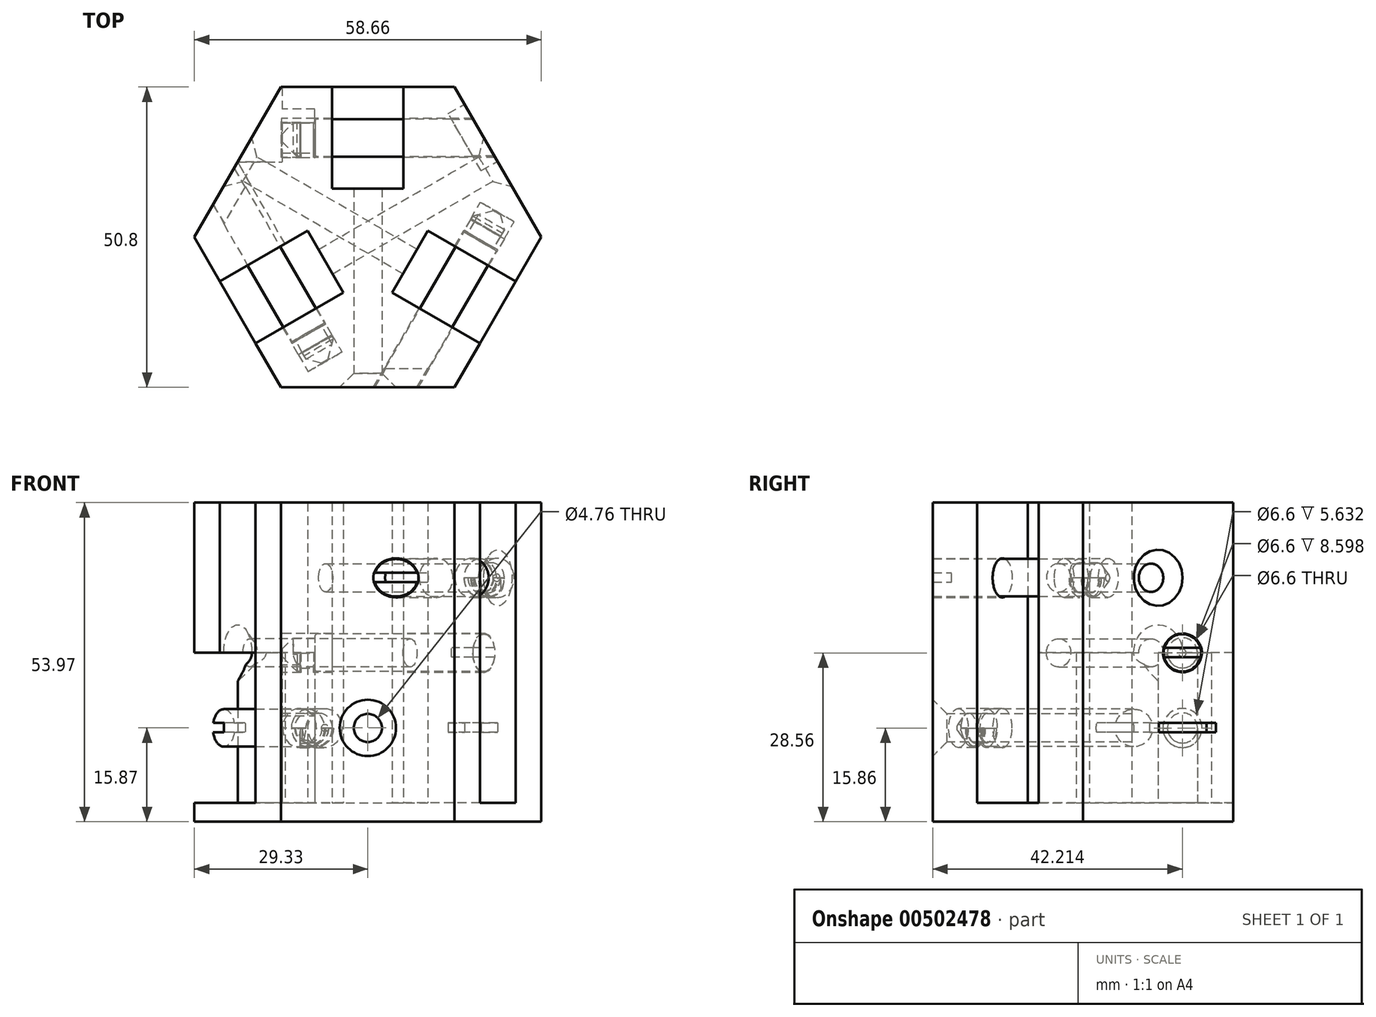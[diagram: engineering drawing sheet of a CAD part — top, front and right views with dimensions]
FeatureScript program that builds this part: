
annotation { "Feature Type Name" : "Feature", "Feature Type Description" : "" }
export const myFeature = defineFeature(function(context is Context, id is Id, definition is map)
    precondition{}
    {
        {
            var Q0;
            Q0=qCreatedBy(makeId("Top.planeOp"),FACE);
            var sketch = newSketch(context, id + "F0", { "sketchPlane" : qUnion([Q0])});
            skCircle(sketch, "E0.cCircle", {"center": v(0, 0) * mm, "radius": 25.4 * mm, "construction": true});
            skLineSegment(sketch, "E0.0", {"start": v(-14.66, 25.4) * mm, "end": v(14.66, 25.4) * mm});
            skLineSegment(sketch, "E0.1", {"start": v(14.66, 25.4) * mm, "end": v(29.33, 0) * mm});
            skLineSegment(sketch, "E0.2", {"start": v(29.33, 0) * mm, "end": v(14.66, -25.4) * mm});
            skLineSegment(sketch, "E0.3", {"start": v(14.66, -25.4) * mm, "end": v(-14.66, -25.4) * mm});
            skLineSegment(sketch, "E0.4", {"start": v(-14.66, -25.4) * mm, "end": v(-29.33, 0) * mm});
            skLineSegment(sketch, "E0.5", {"start": v(-29.33, 0) * mm, "end": v(-14.66, 25.4) * mm});
            skPoint(sketch, "E0.0.midPoint", {"position": v(0, 25.4) * mm});
            skLineSegment(sketch, "E1.0", {"start": v(0, -25.4) * mm, "end": v(-22, 12.7) * mm});
            skLineSegment(sketch, "E1.1", {"start": v(-22, 12.7) * mm, "end": v(22, 12.7) * mm});
            skLineSegment(sketch, "E1.2", {"start": v(22, 12.7) * mm, "end": v(0, -25.4) * mm});
            skLineSegment(sketch, "E2", {"start": v(0, 0) * mm, "end": v(11, -6.35) * mm, "construction": true});
            skLineSegment(sketch, "E3", {"start": v(0, 0) * mm, "end": v(0, 12.7) * mm, "construction": true});
            skLineSegment(sketch, "E4", {"start": v(0, 0) * mm, "end": v(-11, -6.35) * mm, "construction": true});
            skLineSegment(sketch, "E5", {"start": v(-25.01, -7.48) * mm, "end": v(-6.03, 3.48) * mm});
            skLineSegment(sketch, "E6", {"start": v(25.01, -7.48) * mm, "end": v(6.03, 3.48) * mm});
            skLineSegment(sketch, "E7", {"start": v(18.98, -17.92) * mm, "end": v(0, -6.97) * mm});
            skLineSegment(sketch, "E8", {"start": v(0, -6.97) * mm, "end": v(-18.98, -17.92) * mm});
            skLineSegment(sketch, "E9", {"start": v(-6.03, 3.48) * mm, "end": v(-6.03, 25.4) * mm});
            skLineSegment(sketch, "E10", {"start": v(6.03, 3.48) * mm, "end": v(6.03, 25.4) * mm});
            skCircle(sketch, "E11.cCircle", {"center": v(0, 0) * mm, "radius": 6.97 * mm, "construction": true});
            skLineSegment(sketch, "E11.0", {"start": v(0, -6.97) * mm, "end": v(-6.03, 3.48) * mm});
            skLineSegment(sketch, "E11.1", {"start": v(-6.03, 3.48) * mm, "end": v(6.03, 3.48) * mm});
            skLineSegment(sketch, "E11.2", {"start": v(6.03, 3.48) * mm, "end": v(0, -6.97) * mm});
            skLineSegment(sketch, "E12", {"start": v(-10.16, 1.1) * mm, "end": v(-4.12, -9.35) * mm});
            skLineSegment(sketch, "E13", {"start": v(4.12, -9.35) * mm, "end": v(10.16, 1.1) * mm});
            skLineSegment(sketch, "E14", {"start": v(-6.03, 8.25) * mm, "end": v(6.03, 8.25) * mm});
            skSolve(sketch);
        }
        {
            var Q0;
            {var subQ0=sQuery(id+"F0.wireOp",EDGE,"E9");var subQ1=sQuery(id+"F0.wireOp",EDGE,"E0.0");var subQ2=makeQuery(id+"F0.imprint","INTERSECT",VERTEX,{"derivedFrom":[subQ1,subQ0]});Q0=makeQuery(id+"F0.imprint","IMPRINT",FACE,{"disambiguationData":[TD([[makeQuery(id+"F0.imprint","IMPRINT",EDGE,{"disambiguationData":[TD([[subQ2,-1.0]])],"derivedFrom":subQ1}),-1.0]])]});}
            var Q1;
            {var subQ5=sQuery(id+"F0.wireOp",EDGE,"E11.1");Q1=makeQuery(id+"F0.imprint","IMPRINT",FACE,{"disambiguationData":[TD([[makeQuery(id+"F0.imprint","IMPRINT",EDGE,{"derivedFrom":subQ5}),1.0]])]});}
            var Q2;
            {var subQ0=sQuery(id+"F0.wireOp",EDGE,"E0.1");var subQ1=sQuery(id+"F0.wireOp",EDGE,"E0.0");var subQ2=makeQuery(id+"F0.imprint","INTERSECT",VERTEX,{"derivedFrom":[subQ1,subQ0]});Q2=makeQuery(id+"F0.imprint","IMPRINT",FACE,{"disambiguationData":[TD([[makeQuery(id+"F0.imprint","IMPRINT",EDGE,{"disambiguationData":[TD([[subQ2,1.0]])],"derivedFrom":subQ1}),-1.0]])]});}
            var Q3;
            {var subQ1=sQuery(id+"F0.wireOp",EDGE,"E1.1");var subQ3=sQuery(id+"F0.wireOp",EDGE,"E10");var subQ4=makeQuery(id+"F0.imprint","INTERSECT",VERTEX,{"derivedFrom":[subQ1,subQ3]});Q3=makeQuery(id+"F0.imprint","IMPRINT",FACE,{"disambiguationData":[TD([[makeQuery(id+"F0.imprint","IMPRINT",EDGE,{"disambiguationData":[TD([[subQ4,-1.0]])],"derivedFrom":subQ1}),-1.0]])]});}
            var Q4;
            {var subQ0=sQuery(id+"F0.wireOp",EDGE,"E0.2");var subQ1=sQuery(id+"F0.wireOp",EDGE,"E0.1");var subQ2=makeQuery(id+"F0.imprint","INTERSECT",VERTEX,{"derivedFrom":[subQ1,subQ0]});Q4=makeQuery(id+"F0.imprint","IMPRINT",FACE,{"disambiguationData":[TD([[makeQuery(id+"F0.imprint","IMPRINT",EDGE,{"disambiguationData":[TD([[subQ2,-1.0]])],"derivedFrom":subQ0}),-1.0]])]});}
            var Q5;
            {var subQ0=sQuery(id+"F0.wireOp",EDGE,"E6");var subQ1=sQuery(id+"F0.wireOp",EDGE,"E0.2");var subQ2=makeQuery(id+"F0.imprint","INTERSECT",VERTEX,{"derivedFrom":[subQ1,subQ0]});Q5=makeQuery(id+"F0.imprint","IMPRINT",FACE,{"disambiguationData":[TD([[makeQuery(id+"F0.imprint","IMPRINT",EDGE,{"disambiguationData":[TD([[subQ2,-1.0]])],"derivedFrom":subQ1}),-1.0]])]});}
            var Q6;
            {var subQ1=sQuery(id+"F0.wireOp",EDGE,"E1.0");var subQ3=sQuery(id+"F0.wireOp",EDGE,"E8");var subQ4=makeQuery(id+"F0.imprint","INTERSECT",VERTEX,{"derivedFrom":[subQ1,subQ3]});Q6=makeQuery(id+"F0.imprint","IMPRINT",FACE,{"disambiguationData":[TD([[makeQuery(id+"F0.imprint","IMPRINT",EDGE,{"disambiguationData":[TD([[subQ4,1.0]])],"derivedFrom":subQ1}),-1.0]])]});}
            var Q7;
            {var subQ0=sQuery(id+"F0.wireOp",EDGE,"E5");var subQ1=sQuery(id+"F0.wireOp",EDGE,"E0.4");var subQ2=makeQuery(id+"F0.imprint","INTERSECT",VERTEX,{"derivedFrom":[subQ1,subQ0]});Q7=makeQuery(id+"F0.imprint","IMPRINT",FACE,{"disambiguationData":[TD([[makeQuery(id+"F0.imprint","IMPRINT",EDGE,{"disambiguationData":[TD([[subQ2,1.0]])],"derivedFrom":subQ1}),-1.0]])]});}
            var Q8;
            {var subQ0=sQuery(id+"F0.wireOp",EDGE,"E0.5");var subQ1=sQuery(id+"F0.wireOp",EDGE,"E0.4");var subQ2=makeQuery(id+"F0.imprint","INTERSECT",VERTEX,{"derivedFrom":[subQ1,subQ0]});Q8=makeQuery(id+"F0.imprint","IMPRINT",FACE,{"disambiguationData":[TD([[makeQuery(id+"F0.imprint","IMPRINT",EDGE,{"disambiguationData":[TD([[subQ2,1.0]])],"derivedFrom":subQ1}),-1.0]])]});}
            var Q9;
            {var subQ0=sQuery(id+"F0.wireOp",EDGE,"E0.5");var subQ1=sQuery(id+"F0.wireOp",EDGE,"E0.0");var subQ2=makeQuery(id+"F0.imprint","INTERSECT",VERTEX,{"derivedFrom":[subQ1,subQ0]});Q9=makeQuery(id+"F0.imprint","IMPRINT",FACE,{"disambiguationData":[TD([[makeQuery(id+"F0.imprint","IMPRINT",EDGE,{"disambiguationData":[TD([[subQ2,-1.0]])],"derivedFrom":subQ1}),-1.0]])]});}
            var Q10;
            {var subQ0=sQuery(id+"F0.wireOp",EDGE,"E0.4");var subQ1=sQuery(id+"F0.wireOp",EDGE,"E0.3");var subQ2=makeQuery(id+"F0.imprint","INTERSECT",VERTEX,{"derivedFrom":[subQ1,subQ0]});Q10=makeQuery(id+"F0.imprint","IMPRINT",FACE,{"disambiguationData":[TD([[makeQuery(id+"F0.imprint","IMPRINT",EDGE,{"disambiguationData":[TD([[subQ2,-1.0]])],"derivedFrom":subQ0}),-1.0]])]});}
            var Q11;
            {var subQ0=sQuery(id+"F0.wireOp",EDGE,"E0.3");var subQ1=sQuery(id+"F0.wireOp",EDGE,"E0.2");var subQ2=makeQuery(id+"F0.imprint","INTERSECT",VERTEX,{"derivedFrom":[subQ1,subQ0]});Q11=makeQuery(id+"F0.imprint","IMPRINT",FACE,{"disambiguationData":[TD([[makeQuery(id+"F0.imprint","IMPRINT",EDGE,{"disambiguationData":[TD([[subQ2,1.0]])],"derivedFrom":subQ1}),-1.0]])]});}
            var Q12;
            {var subQ1=sQuery(id+"F0.wireOp",EDGE,"E1.0");var subQ3=sQuery(id+"F0.wireOp",EDGE,"E5");var subQ4=makeQuery(id+"F0.imprint","INTERSECT",VERTEX,{"derivedFrom":[subQ1,subQ3]});Q12=makeQuery(id+"F0.imprint","IMPRINT",FACE,{"disambiguationData":[TD([[makeQuery(id+"F0.imprint","IMPRINT",EDGE,{"disambiguationData":[TD([[subQ4,-1.0]])],"derivedFrom":subQ1}),-1.0]])]});}
            var Q13;
            {var subQ5=sQuery(id+"F0.wireOp",EDGE,"E11.0");Q13=makeQuery(id+"F0.imprint","IMPRINT",FACE,{"disambiguationData":[TD([[makeQuery(id+"F0.imprint","IMPRINT",EDGE,{"derivedFrom":subQ5}),1.0]])]});}
            var Q14;
            {var subQ5=sQuery(id+"F0.wireOp",EDGE,"E11.2");Q14=makeQuery(id+"F0.imprint","IMPRINT",FACE,{"disambiguationData":[TD([[makeQuery(id+"F0.imprint","IMPRINT",EDGE,{"derivedFrom":subQ5}),1.0]])]});}
            var Q15;
            Q15=makeQuery(id+"F0.imprint","IMPRINT",FACE,{"disambiguationData":[TD([[makeQuery(id+"F0.imprint","IMPRINT",EDGE,{"derivedFrom":sQuery(id+"F0.wireOp",EDGE,"E11.0")}),-1.0]])]});
            var Q16;
            Q16=makeQuery(id+"F2.opExtrude","SWEPT_FACE",FACE,{"disambiguationData":[OSD([sQuery(id+"F0.wireOp",EDGE,"E6")])]});
            var Q17;
            {var subQ5=sQuery(id+"F0.wireOp",EDGE,"E14");Q17=makeQuery(id+"F0.imprint","IMPRINT",FACE,{"disambiguationData":[TD([[makeQuery(id+"F0.imprint","IMPRINT",EDGE,{"derivedFrom":subQ5}),1.0]])]});}
            var Q18;
            {var subQ5=sQuery(id+"F0.wireOp",EDGE,"E13");Q18=makeQuery(id+"F0.imprint","IMPRINT",FACE,{"disambiguationData":[TD([[makeQuery(id+"F0.imprint","IMPRINT",EDGE,{"derivedFrom":subQ5}),-1.0]])]});}
            var Q19;
            {var subQ5=sQuery(id+"F0.wireOp",EDGE,"E12");Q19=makeQuery(id+"F0.imprint","IMPRINT",FACE,{"disambiguationData":[TD([[makeQuery(id+"F0.imprint","IMPRINT",EDGE,{"derivedFrom":subQ5}),-1.0]])]});}
            extrude(context, id + "F1", {"entities" : qUnion([Q0, Q1, Q2, Q3, Q4, Q5, Q6, Q7, Q8, Q9, Q10, Q11, Q12, Q13, Q14, Q15, Q16, Q17, Q18, Q19]), "oppositeDirection" : true, "depth" : 3.17 * mm});
        }
        {
            var Q0;
            {var subQ0=sQuery(id+"F0.wireOp",EDGE,"E0.5");var subQ1=sQuery(id+"F0.wireOp",EDGE,"E0.0");var subQ2=makeQuery(id+"F0.imprint","INTERSECT",VERTEX,{"derivedFrom":[subQ1,subQ0]});Q0=makeQuery(id+"F0.imprint","IMPRINT",FACE,{"disambiguationData":[TD([[makeQuery(id+"F0.imprint","IMPRINT",EDGE,{"disambiguationData":[TD([[subQ2,-1.0]])],"derivedFrom":subQ1}),-1.0]])]});}
            var Q1;
            {var subQ0=sQuery(id+"F0.wireOp",EDGE,"E0.1");var subQ1=sQuery(id+"F0.wireOp",EDGE,"E0.0");var subQ2=makeQuery(id+"F0.imprint","INTERSECT",VERTEX,{"derivedFrom":[subQ1,subQ0]});Q1=makeQuery(id+"F0.imprint","IMPRINT",FACE,{"disambiguationData":[TD([[makeQuery(id+"F0.imprint","IMPRINT",EDGE,{"disambiguationData":[TD([[subQ2,1.0]])],"derivedFrom":subQ1}),-1.0]])]});}
            var Q2;
            {var subQ0=sQuery(id+"F0.wireOp",EDGE,"E0.2");var subQ1=sQuery(id+"F0.wireOp",EDGE,"E0.1");var subQ2=makeQuery(id+"F0.imprint","INTERSECT",VERTEX,{"derivedFrom":[subQ1,subQ0]});Q2=makeQuery(id+"F0.imprint","IMPRINT",FACE,{"disambiguationData":[TD([[makeQuery(id+"F0.imprint","IMPRINT",EDGE,{"disambiguationData":[TD([[subQ2,-1.0]])],"derivedFrom":subQ0}),-1.0]])]});}
            var Q3;
            {var subQ0=sQuery(id+"F0.wireOp",EDGE,"E0.5");var subQ1=sQuery(id+"F0.wireOp",EDGE,"E0.4");var subQ2=makeQuery(id+"F0.imprint","INTERSECT",VERTEX,{"derivedFrom":[subQ1,subQ0]});Q3=makeQuery(id+"F0.imprint","IMPRINT",FACE,{"disambiguationData":[TD([[makeQuery(id+"F0.imprint","IMPRINT",EDGE,{"disambiguationData":[TD([[subQ2,1.0]])],"derivedFrom":subQ1}),-1.0]])]});}
            var Q4;
            {var subQ1=sQuery(id+"F0.wireOp",EDGE,"E1.1");var subQ3=sQuery(id+"F0.wireOp",EDGE,"E10");var subQ4=makeQuery(id+"F0.imprint","INTERSECT",VERTEX,{"derivedFrom":[subQ1,subQ3]});Q4=makeQuery(id+"F0.imprint","IMPRINT",FACE,{"disambiguationData":[TD([[makeQuery(id+"F0.imprint","IMPRINT",EDGE,{"disambiguationData":[TD([[subQ4,-1.0]])],"derivedFrom":subQ1}),-1.0]])]});}
            var Q5;
            {var subQ1=sQuery(id+"F0.wireOp",EDGE,"E1.0");var subQ3=sQuery(id+"F0.wireOp",EDGE,"E5");var subQ4=makeQuery(id+"F0.imprint","INTERSECT",VERTEX,{"derivedFrom":[subQ1,subQ3]});Q5=makeQuery(id+"F0.imprint","IMPRINT",FACE,{"disambiguationData":[TD([[makeQuery(id+"F0.imprint","IMPRINT",EDGE,{"disambiguationData":[TD([[subQ4,-1.0]])],"derivedFrom":subQ1}),-1.0]])]});}
            var Q6;
            {var subQ1=sQuery(id+"F0.wireOp",EDGE,"E1.0");var subQ3=sQuery(id+"F0.wireOp",EDGE,"E8");var subQ4=makeQuery(id+"F0.imprint","INTERSECT",VERTEX,{"derivedFrom":[subQ1,subQ3]});Q6=makeQuery(id+"F0.imprint","IMPRINT",FACE,{"disambiguationData":[TD([[makeQuery(id+"F0.imprint","IMPRINT",EDGE,{"disambiguationData":[TD([[subQ4,1.0]])],"derivedFrom":subQ1}),-1.0]])]});}
            var Q7;
            {var subQ0=sQuery(id+"F0.wireOp",EDGE,"E0.3");var subQ1=sQuery(id+"F0.wireOp",EDGE,"E0.2");var subQ2=makeQuery(id+"F0.imprint","INTERSECT",VERTEX,{"derivedFrom":[subQ1,subQ0]});Q7=makeQuery(id+"F0.imprint","IMPRINT",FACE,{"disambiguationData":[TD([[makeQuery(id+"F0.imprint","IMPRINT",EDGE,{"disambiguationData":[TD([[subQ2,1.0]])],"derivedFrom":subQ1}),-1.0]])]});}
            var Q8;
            {var subQ0=sQuery(id+"F0.wireOp",EDGE,"E0.4");var subQ1=sQuery(id+"F0.wireOp",EDGE,"E0.3");var subQ2=makeQuery(id+"F0.imprint","INTERSECT",VERTEX,{"derivedFrom":[subQ1,subQ0]});Q8=makeQuery(id+"F0.imprint","IMPRINT",FACE,{"disambiguationData":[TD([[makeQuery(id+"F0.imprint","IMPRINT",EDGE,{"disambiguationData":[TD([[subQ2,-1.0]])],"derivedFrom":subQ0}),-1.0]])]});}
            var Q9;
            {var subQ0=sQuery(id+"F0.wireOp",EDGE,"E11.0");Q9=makeQuery(id+"F0.imprint","IMPRINT",FACE,{"disambiguationData":[TD([[makeQuery(id+"F0.imprint","IMPRINT",EDGE,{"derivedFrom":subQ0}),1.0]])]});}
            var Q10;
            {var subQ0=sQuery(id+"F0.wireOp",EDGE,"E11.2");Q10=makeQuery(id+"F0.imprint","IMPRINT",FACE,{"disambiguationData":[TD([[makeQuery(id+"F0.imprint","IMPRINT",EDGE,{"derivedFrom":subQ0}),1.0]])]});}
            var Q11;
            {var subQ0=sQuery(id+"F0.wireOp",EDGE,"E11.1");Q11=makeQuery(id+"F0.imprint","IMPRINT",FACE,{"disambiguationData":[TD([[makeQuery(id+"F0.imprint","IMPRINT",EDGE,{"derivedFrom":subQ0}),1.0]])]});}
            var Q12;
            Q12=makeQuery(id+"F0.imprint","IMPRINT",FACE,{"disambiguationData":[TD([[makeQuery(id+"F0.imprint","IMPRINT",EDGE,{"derivedFrom":sQuery(id+"F0.wireOp",EDGE,"E11.0")}),-1.0]])]});
            extrude(context, id + "F2", {"entities" : qUnion([Q0, Q1, Q2, Q3, Q4, Q5, Q6, Q7, Q8, Q9, Q10, Q11, Q12]), "operationType" : NewBodyOperationType.ADD, "depth" : 50.8 * mm});
        }
        {
            var Q0;
            {var subQ0=sQuery(id+"F0.wireOp",EDGE,"E0.3");Q0=makeQuery(id+"F2.boolean.opBoolean","MERGE",FACE,{"derivedFrom":[makeQuery(id+"F1.opExtrude","SWEPT_FACE",FACE,{"disambiguationData":[OSD([subQ0])]}),makeQuery(id+"F2.opExtrude","SWEPT_FACE",FACE,{"disambiguationData":[OSD([subQ0])]})]});}
            var sketch = newSketch(context, id + "F3", { "sketchPlane" : qUnion([Q0])});
            skPoint(sketch, "E15", {"position": v(0, 12.7) * mm});
            skSolve(sketch);
        }
        {
            var Q0;
            {var subQ0=sQuery(id+"F0.wireOp",EDGE,"E0.1");Q0=makeQuery(id+"F2.boolean.opBoolean","MERGE",FACE,{"derivedFrom":[makeQuery(id+"F1.opExtrude","SWEPT_FACE",FACE,{"disambiguationData":[OSD([subQ0])]}),makeQuery(id+"F2.opExtrude","SWEPT_FACE",FACE,{"disambiguationData":[OSD([subQ0])]})]});}
            var sketch = newSketch(context, id + "F4", { "sketchPlane" : qUnion([Q0])});
            skPoint(sketch, "E16", {"position": v(0, 38.1) * mm});
            skPoint(sketch, "E16.positionSnap0", {"position": v(-14.66, 23.81) * mm});
            skSolve(sketch);
        }
        {
            var Q0;
            {var subQ0=sQuery(id+"F0.wireOp",EDGE,"E0.5");Q0=makeQuery(id+"F2.boolean.opBoolean","MERGE",FACE,{"derivedFrom":[makeQuery(id+"F1.opExtrude","SWEPT_FACE",FACE,{"disambiguationData":[OSD([subQ0])]}),makeQuery(id+"F2.opExtrude","SWEPT_FACE",FACE,{"disambiguationData":[OSD([subQ0])]})]});}
            var sketch = newSketch(context, id + "F5", { "sketchPlane" : qUnion([Q0])});
            skPoint(sketch, "E17", {"position": v(0, 25.4) * mm});
            skPoint(sketch, "E17.positionSnap0", {"position": v(-14.66, 23.81) * mm});
            skPoint(sketch, "E17.positionSnap1", {"position": v(0, 50.8) * mm});
            skSolve(sketch);
        }
        {
            var Q0;
            Q0=sQuery(id+"F3.wireOp",VERTEX,"E15");
            var Q1;
            Q1=sQuery(id+"F4.wireOp",VERTEX,"E16");
            var Q2;
            Q2=sQuery(id+"F5.wireOp",VERTEX,"E17");
            var Q3;
            Q3=makeQuery(id+"F1.opExtrude","SWEPT_BODY",BODY,{"disambiguationData":[OSD([sQuery(id+"F0.wireOp",EDGE,"E0.0"),sQuery(id+"F0.wireOp",EDGE,"E0.1"),sQuery(id+"F0.wireOp",EDGE,"E0.2"),sQuery(id+"F0.wireOp",EDGE,"E0.3"),sQuery(id+"F0.wireOp",EDGE,"E0.4"),sQuery(id+"F0.wireOp",EDGE,"E0.5")])]});
            hole(context, id + "F6", {"style" : HoleStyle.C_SINK, "endStyle" : HoleEndStyle.THROUGH, "holeDiameter" : 4.76 * mm, "cSinkDiameter" : 9.52 * mm, "cSinkAngle" : 90 * degree, "isTappedThrough" : true, "tappedDepth" : 12.7 * mm, "tapClearance" : 3, "locations" : qUnion([Q0, Q1, Q2]), "scope" : qUnion([Q3])});
        }
        {
            var Q0;
            Q0=qCreatedBy(makeId("Right.planeOp"),FACE);
            var sketch = newSketch(context, id + "F7", { "sketchPlane" : qUnion([Q0])});
            skCircle(sketch, "E18", {"center": v(16.81, 12.7) * mm, "radius": 3.18 * mm});
            skLineSegment(sketch, "E19", {"start": v(8.24, 12.7) * mm, "end": v(25.39, 12.7) * mm, "construction": true});
            skLineSegment(sketch, "E20", {"start": v(0, 57.97) * mm, "end": v(0, -40.67) * mm, "construction": true});
            skSolve(sketch);
        }
        {
            var Q0;
            Q0=makeQuery(id+"F7.imprint","IMPRINT",FACE,{"disambiguationData":[TD([[makeQuery(id+"F7.imprint","IMPRINT",EDGE,{"derivedFrom":sQuery(id+"F7.wireOp",EDGE,"E18")}),1.0]])]});
            extrude(context, id + "F8", {"entities" : qUnion([Q0]), "endBound" : BoundingType.SYMMETRIC, "depth" : 76.2 * mm});
        }
        {
            var Q0;
            Q0=qCreatedBy(makeId("Top.planeOp"),FACE);
            var sketch = newSketch(context, id + "F9", { "sketchPlane" : qUnion([Q0])});
            skCircle(sketch, "E21.cCircle", {"center": v(0, 0) * mm, "radius": 25.4 * mm, "construction": true});
            skLineSegment(sketch, "E21.0", {"start": v(-14.66, 25.4) * mm, "end": v(14.66, 25.4) * mm});
            skLineSegment(sketch, "E21.1", {"start": v(14.66, 25.4) * mm, "end": v(29.33, 0) * mm});
            skLineSegment(sketch, "E21.2", {"start": v(29.33, 0) * mm, "end": v(14.66, -25.4) * mm});
            skLineSegment(sketch, "E21.3", {"start": v(14.66, -25.4) * mm, "end": v(-14.66, -25.4) * mm});
            skLineSegment(sketch, "E21.4", {"start": v(-14.66, -25.4) * mm, "end": v(-29.33, 0) * mm});
            skLineSegment(sketch, "E21.5", {"start": v(-29.33, 0) * mm, "end": v(-14.66, 25.4) * mm});
            skPoint(sketch, "E21.0.midPoint", {"position": v(0, 25.4) * mm});
            skLineSegment(sketch, "E22.0", {"start": v(0, -25.4) * mm, "end": v(-22, 12.7) * mm});
            skLineSegment(sketch, "E22.1", {"start": v(-22, 12.7) * mm, "end": v(22, 12.7) * mm});
            skLineSegment(sketch, "E22.2", {"start": v(22, 12.7) * mm, "end": v(0, -25.4) * mm});
            skLineSegment(sketch, "E23", {"start": v(0, 0) * mm, "end": v(11, -6.35) * mm, "construction": true});
            skLineSegment(sketch, "E24", {"start": v(0, 0) * mm, "end": v(0, 12.7) * mm, "construction": true});
            skLineSegment(sketch, "E25", {"start": v(0, 0) * mm, "end": v(-11, -6.35) * mm, "construction": true});
            skLineSegment(sketch, "E26", {"start": v(-25.01, -7.48) * mm, "end": v(-6.03, 3.48) * mm});
            skLineSegment(sketch, "E27", {"start": v(25.01, -7.48) * mm, "end": v(6.03, 3.48) * mm});
            skLineSegment(sketch, "E28", {"start": v(18.98, -17.92) * mm, "end": v(0, -6.97) * mm});
            skLineSegment(sketch, "E29", {"start": v(0, -6.97) * mm, "end": v(-18.98, -17.92) * mm});
            skLineSegment(sketch, "E30", {"start": v(-6.03, 3.48) * mm, "end": v(-6.03, 25.4) * mm});
            skLineSegment(sketch, "E31", {"start": v(6.03, 3.48) * mm, "end": v(6.03, 25.4) * mm});
            skCircle(sketch, "E32.cCircle", {"center": v(0, 0) * mm, "radius": 6.97 * mm, "construction": true});
            skLineSegment(sketch, "E32.0", {"start": v(0, -6.97) * mm, "end": v(-6.03, 3.48) * mm});
            skLineSegment(sketch, "E32.1", {"start": v(-6.03, 3.48) * mm, "end": v(6.03, 3.48) * mm});
            skLineSegment(sketch, "E32.2", {"start": v(6.03, 3.48) * mm, "end": v(0, -6.97) * mm});
            skLineSegment(sketch, "E33", {"start": v(-10.16, 1.1) * mm, "end": v(-4.12, -9.35) * mm});
            skLineSegment(sketch, "E34", {"start": v(4.12, -9.35) * mm, "end": v(10.16, 1.1) * mm});
            skLineSegment(sketch, "E35", {"start": v(-6.03, 8.25) * mm, "end": v(6.03, 8.25) * mm});
            skLineSegment(sketch, "E36.bottom", {"start": v(-66.37, 54.44) * mm, "end": v(74.44, 54.44) * mm});
            skLineSegment(sketch, "E36.top", {"start": v(-66.37, -46.28) * mm, "end": v(74.44, -46.28) * mm});
            skLineSegment(sketch, "E36.left", {"start": v(-66.37, 54.44) * mm, "end": v(-66.37, -46.28) * mm});
            skLineSegment(sketch, "E36.right", {"start": v(74.44, 54.44) * mm, "end": v(74.44, -46.28) * mm});
            skLineSegment(sketch, "E37", {"start": v(-14.52, 25.4) * mm, "end": v(-14.52, 12.7) * mm});
            skLineSegment(sketch, "E38", {"start": v(-38.88, 19.38) * mm, "end": v(-8.95, 19.38) * mm});
            skLineSegment(sketch, "E39", {"start": v(-8.95, 19.26) * mm, "end": v(-8.95, 21.69) * mm});
            skLineSegment(sketch, "E40", {"start": v(-8.95, 21.69) * mm, "end": v(-38.94, 21.69) * mm});
            skLineSegment(sketch, "E41", {"start": v(-38.94, 21.69) * mm, "end": v(-38.88, 19.38) * mm});
            skLineSegment(sketch, "E42", {"start": v(-8.95, 19.38) * mm, "end": v(-8.95, 13.78) * mm});
            skLineSegment(sketch, "E43", {"start": v(-8.95, 13.78) * mm, "end": v(-11.38, 13.78) * mm});
            skLineSegment(sketch, "E44", {"start": v(-11.38, 13.78) * mm, "end": v(-11.38, 19.38) * mm});
            skLineSegment(sketch, "E45.bottom", {"start": v(-8.95, 21.69) * mm, "end": v(-20.9, 21.69) * mm});
            skLineSegment(sketch, "E45.top", {"start": v(-8.95, 19.38) * mm, "end": v(-20.9, 19.38) * mm});
            skLineSegment(sketch, "E45.left", {"start": v(-8.95, 21.69) * mm, "end": v(-8.95, 19.38) * mm});
            skLineSegment(sketch, "E45.right", {"start": v(-20.9, 21.69) * mm, "end": v(-20.9, 19.38) * mm});
            skLineSegment(sketch, "E46.top", {"start": v(-8.95, 21.69) * mm, "end": v(-11.38, 21.69) * mm});
            skLineSegment(sketch, "E46.left", {"start": v(-8.95, 13.78) * mm, "end": v(-8.95, 21.69) * mm});
            skLineSegment(sketch, "E46.right", {"start": v(-11.38, 13.78) * mm, "end": v(-11.38, 21.69) * mm});
            skSolve(sketch);
        }
        {
            var Q0;
            Q0=qCreatedBy(makeId("Right.planeOp"),FACE);
            var sketch = newSketch(context, id + "F10", { "sketchPlane" : qUnion([Q0])});
            skCircle(sketch, "E47", {"center": v(16.81, 12.69) * mm, "radius": 2.54 * mm});
            skLineSegment(sketch, "E48", {"start": v(8.24, 12.69) * mm, "end": v(25.39, 12.69) * mm, "construction": true});
            skLineSegment(sketch, "E49", {"start": v(-11.2, 46.62) * mm, "end": v(-11.2, -52.02) * mm, "construction": true});
            skCircle(sketch, "E50", {"center": v(16.81, 12.69) * mm, "radius": 3.3 * mm});
            skLineSegment(sketch, "E51", {"start": v(16.81, 16) * mm, "end": v(16.81, 9.39) * mm});
            skLineSegment(sketch, "E52", {"start": v(20.18, 12.69) * mm, "end": v(20.12, 12.69) * mm});
            skLineSegment(sketch, "E53", {"start": v(20.12, 12.69) * mm, "end": v(13.51, 12.69) * mm});
            skSolve(sketch);
        }
        {
            var Q0;
            {var subQ0=sQuery(id+"F10.wireOp",EDGE,"E51");var subQ1=sQuery(id+"F10.wireOp",EDGE,"E47");var subQ2=makeQuery(id+"F10.imprint","INTERSECT",VERTEX,{"disambiguationData":[OD(0.0)],"derivedFrom":[subQ1,subQ0]});Q0=makeQuery(id+"F10.imprint","IMPRINT",FACE,{"disambiguationData":[TD([[makeQuery(id+"F10.imprint","IMPRINT",EDGE,{"disambiguationData":[TD([[subQ2,-1.0]])],"derivedFrom":subQ1}),-1.0]])]});}
            var Q1;
            {var subQ0=sQuery(id+"F10.wireOp",EDGE,"E51");var subQ1=sQuery(id+"F10.wireOp",EDGE,"E47");var subQ2=makeQuery(id+"F10.imprint","INTERSECT",VERTEX,{"disambiguationData":[OD(0.0)],"derivedFrom":[subQ1,subQ0]});Q1=makeQuery(id+"F10.imprint","IMPRINT",FACE,{"disambiguationData":[TD([[makeQuery(id+"F10.imprint","IMPRINT",EDGE,{"disambiguationData":[TD([[subQ2,1.0]])],"derivedFrom":subQ1}),-1.0]])]});}
            extrude(context, id + "F11", {"entities" : qUnion([Q0, Q1]), "operationType" : NewBodyOperationType.REMOVE, "oppositeDirection" : true, "depth" : 16.92 * mm, "hasSecondDirection" : true, "secondDirectionOppositeDirection" : true, "secondDirectionDepth" : 8.9 * mm});
        }
        {
            var Q0;
            {var subQ0=sQuery(id+"F10.wireOp",EDGE,"E53");var subQ1=sQuery(id+"F10.wireOp",EDGE,"E47");var subQ2=makeQuery(id+"F10.imprint","INTERSECT",VERTEX,{"disambiguationData":[OD(1.0)],"derivedFrom":[subQ1,subQ0]});Q0=makeQuery(id+"F10.imprint","IMPRINT",FACE,{"disambiguationData":[TD([[makeQuery(id+"F10.imprint","IMPRINT",EDGE,{"disambiguationData":[TD([[subQ2,-1.0]])],"derivedFrom":subQ1}),-1.0]])]});}
            var Q1;
            {var subQ0=sQuery(id+"F10.wireOp",EDGE,"E53");var subQ1=sQuery(id+"F10.wireOp",EDGE,"E47");var subQ2=makeQuery(id+"F10.imprint","INTERSECT",VERTEX,{"disambiguationData":[OD(0.0)],"derivedFrom":[subQ1,subQ0]});Q1=makeQuery(id+"F10.imprint","IMPRINT",FACE,{"disambiguationData":[TD([[makeQuery(id+"F10.imprint","IMPRINT",EDGE,{"disambiguationData":[TD([[subQ2,1.0]])],"derivedFrom":subQ1}),-1.0]])]});}
            extrude(context, id + "F12", {"entities" : qUnion([Q0, Q1]), "operationType" : NewBodyOperationType.REMOVE, "oppositeDirection" : true, "depth" : 11.43 * mm, "hasSecondDirection" : true, "secondDirectionOppositeDirection" : true, "secondDirectionDepth" : 8.9 * mm});
        }
        {
            var Q0;
            Q0=makeQuery(id+"F9.imprint","IMPRINT",FACE,{"disambiguationData":[TD([[makeQuery(id+"F9.imprint","IMPRINT",EDGE,{"derivedFrom":sQuery(id+"F9.wireOp",EDGE,"E36.bottom")}),-1.0]])]});
            var Q1;
            {var subQ5=sQuery(id+"F9.wireOp",EDGE,"E45.right");Q1=makeQuery(id+"F9.imprint","IMPRINT",FACE,{"disambiguationData":[TD([[makeQuery(id+"F9.imprint","IMPRINT",EDGE,{"derivedFrom":subQ5}),1.0]])]});}
            var Q2;
            Q2=makeQuery(id+"F9.imprint","IMPRINT",FACE,{"disambiguationData":[TD([[makeQuery(id+"F9.imprint","IMPRINT",EDGE,{"derivedFrom":sQuery(id+"F9.wireOp",EDGE,"E38")}),1.0]])]});
            var Q3;
            {var subQ0=sQuery(id+"F9.wireOp",EDGE,"E45.top");var subQ1=sQuery(id+"F9.wireOp",EDGE,"E21.5");var subQ2=makeQuery(id+"F9.imprint","INTERSECT",VERTEX,{"derivedFrom":[subQ1,subQ0]});Q3=makeQuery(id+"F9.imprint","IMPRINT",FACE,{"disambiguationData":[TD([[makeQuery(id+"F9.imprint","IMPRINT",EDGE,{"disambiguationData":[TD([[subQ2,-1.0]])],"derivedFrom":subQ1}),-1.0]])]});}
            var Q4;
            {var subQ0=sQuery(id+"F9.wireOp",EDGE,"E22.1");var subQ5=sQuery(id+"F9.wireOp",EDGE,"E37");var subQ6=makeQuery(id+"F9.imprint","INTERSECT",VERTEX,{"derivedFrom":[subQ0,subQ5]});Q4=makeQuery(id+"F9.imprint","IMPRINT",FACE,{"disambiguationData":[TD([[makeQuery(id+"F9.imprint","IMPRINT",EDGE,{"disambiguationData":[TD([[subQ6,1.0]])],"derivedFrom":subQ5}),-1.0]])]});}
            extrude(context, id + "F13", {"entities" : qUnion([Q0, Q1, Q2, Q3, Q4]), "operationType" : NewBodyOperationType.REMOVE, "depth" : 25.4 * mm});
        }
        {
            var Q0;
            Q0=makeQuery(id+"F13.boolean.opBoolean","INTERSECT",EDGE,{"derivedFrom":[makeQuery(id+"F8.opExtrude","SWEPT_FACE",FACE,{"disambiguationData":[OSD([sQuery(id+"F7.wireOp",EDGE,"E18")])]}),makeQuery(id+"F13.opExtrude","SWEPT_FACE",FACE,{"disambiguationData":[OSD([sQuery(id+"F9.wireOp",EDGE,"E37")])]})]});
            chamfer(context, id + "F14", {"entities" : qUnion([Q0]), "width" : 2.54 * mm, "tangentPropagation" : true});
        }
        {
            var Q0;
            Q0=makeQuery(id+"F13.boolean.opBoolean","COPY",FACE,{"derivedFrom":makeQuery(id+"F13.opExtrude","SWEPT_FACE",FACE,{"disambiguationData":[OSD([sQuery(id+"F9.wireOp",EDGE,"E21.1")])]})});
            var sketch = newSketch(context, id + "F15", { "sketchPlane" : qUnion([Q0])});
            skLineSegment(sketch, "E54.bottom", {"start": v(0.16, 13.54) * mm, "end": v(11.3, 13.54) * mm});
            skLineSegment(sketch, "E54.top", {"start": v(0.16, 11.95) * mm, "end": v(11.3, 11.95) * mm});
            skLineSegment(sketch, "E54.left", {"start": v(0.16, 13.54) * mm, "end": v(0.16, 11.95) * mm});
            skLineSegment(sketch, "E54.right", {"start": v(11.3, 13.54) * mm, "end": v(11.3, 11.95) * mm});
            skSolve(sketch);
        }
        {
            var Q0;
            {var subQ0=sQuery(id+"F15.wireOp",EDGE,"E54.left");Q0=makeQuery(id+"F15.imprint","IMPRINT",FACE,{"disambiguationData":[TD([[makeQuery(id+"F15.imprint","IMPRINT",EDGE,{"derivedFrom":subQ0}),1.0]])]});}
            var Q1;
            {var subQ0=sQuery(id+"F15.wireOp",EDGE,"E54.bottom");var subQ1=sQuery(id+"F7.wireOp",EDGE,"E18");var subQ5=makeQuery(id+"F13.boolean.opBoolean","INTERSECT",EDGE,{"derivedFrom":[makeQuery(id+"F12.boolean.opBoolean","SPLIT",FACE,{"disambiguationData":[TD([makeQuery(id+"F8.opExtrude","CAP_FACE",FACE,{"disambiguationData":[OSD([subQ1])],"isStart":false})])],"derivedFrom":makeQuery(id+"F8.opExtrude","SWEPT_FACE",FACE,{"disambiguationData":[OSD([subQ1])]})}),makeQuery(id+"F13.opExtrude","SWEPT_FACE",FACE,{"disambiguationData":[OSD([sQuery(id+"F9.wireOp",EDGE,"E21.1")])]})]});var subQ6=makeQuery(id+"F15.imprint","INTERSECT",VERTEX,{"disambiguationData":[OD(0.0)],"derivedFrom":[subQ5,subQ0]});Q1=makeQuery(id+"F15.imprint","IMPRINT",FACE,{"disambiguationData":[TD([[makeQuery(id+"F15.imprint","IMPRINT",EDGE,{"disambiguationData":[TD([[subQ6,-1.0]])],"derivedFrom":subQ0}),-1.0]])]});}
            var Q2;
            {var subQ0=sQuery(id+"F15.wireOp",EDGE,"E54.right");Q2=makeQuery(id+"F15.imprint","IMPRINT",FACE,{"disambiguationData":[TD([[makeQuery(id+"F15.imprint","IMPRINT",EDGE,{"derivedFrom":subQ0}),-1.0]])]});}
            extrude(context, id + "F16", {"entities" : qUnion([Q0, Q1, Q2]), "operationType" : NewBodyOperationType.REMOVE, "oppositeDirection" : true, "depth" : 3.17 * mm});
        }
        {
            var Q0;
            Q0=makeQuery(id+"F8.opExtrude","SWEPT_BODY",BODY,{"disambiguationData":[OSD([sQuery(id+"F7.wireOp",EDGE,"E18")])]});
            var Q1;
            Q1=sQuery(id+"F7.wireOp",EDGE,"E20");
            circularPattern(context, id + "F17", {"entities" : qUnion([Q0]), "axis" : qUnion([Q1]), "angle" : 360 * degree, "instanceCount" : 3, "equalSpace" : true});
        }
        {
            var Q0;
            Q0=makeQuery(id+"F17.opPattern","COPY",BODY,{"derivedFrom":makeQuery(id+"F8.opExtrude","SWEPT_BODY",BODY,{"disambiguationData":[OSD([sQuery(id+"F7.wireOp",EDGE,"E18")])]}),"instanceName":"1"});
            transform(context, id + "F18", {"entities" : qUnion([Q0]), "transformType" : TransformType.TRANSLATION_3D, "dx" : 0 * mm, "dy" : 0 * mm, "dz" : 25.4 * mm, "makeCopy" : false});
        }
        {
            var Q0;
            Q0=makeQuery(id+"F8.opExtrude","SWEPT_BODY",BODY,{"disambiguationData":[OSD([sQuery(id+"F7.wireOp",EDGE,"E18")])]});
            transform(context, id + "F19", {"entities" : qUnion([Q0]), "transformType" : TransformType.TRANSLATION_3D, "dx" : 0 * mm, "dy" : 0 * mm, "dz" : 12.7 * mm, "makeCopy" : false});
        }
        {
            var Q0;
            {var subQ0=sQuery(id+"F10.wireOp",EDGE,"E53");var subQ3=makeQuery(id+"F10.imprint","IMPRINT",VERTEX,{"derivedFrom":subQ0});Q0=makeQuery(id+"F10.imprint","IMPRINT",FACE,{"disambiguationData":[TD([[makeQuery(id+"F10.imprint","IMPRINT",EDGE,{"disambiguationData":[TD([[subQ3,1.0]])],"derivedFrom":subQ0}),-1.0]])]});}
            var Q1;
            {var subQ0=sQuery(id+"F10.wireOp",EDGE,"E51");var subQ1=sQuery(id+"F10.wireOp",EDGE,"E47");var subQ2=makeQuery(id+"F10.imprint","INTERSECT",VERTEX,{"disambiguationData":[OD(0.0)],"derivedFrom":[subQ1,subQ0]});Q1=makeQuery(id+"F10.imprint","IMPRINT",FACE,{"disambiguationData":[TD([[makeQuery(id+"F10.imprint","IMPRINT",EDGE,{"disambiguationData":[TD([[subQ2,-1.0]])],"derivedFrom":subQ1}),-1.0]])]});}
            var Q2;
            {var subQ0=sQuery(id+"F10.wireOp",EDGE,"E51");var subQ1=sQuery(id+"F10.wireOp",EDGE,"E47");var subQ2=makeQuery(id+"F10.imprint","INTERSECT",VERTEX,{"disambiguationData":[OD(0.0)],"derivedFrom":[subQ1,subQ0]});Q2=makeQuery(id+"F10.imprint","IMPRINT",FACE,{"disambiguationData":[TD([[makeQuery(id+"F10.imprint","IMPRINT",EDGE,{"disambiguationData":[TD([[subQ2,-1.0]])],"derivedFrom":subQ1}),1.0]])]});}
            var Q3;
            {var subQ0=sQuery(id+"F10.wireOp",EDGE,"E51");var subQ1=sQuery(id+"F10.wireOp",EDGE,"E47");var subQ2=makeQuery(id+"F10.imprint","INTERSECT",VERTEX,{"disambiguationData":[OD(0.0)],"derivedFrom":[subQ1,subQ0]});Q3=makeQuery(id+"F10.imprint","IMPRINT",FACE,{"disambiguationData":[TD([[makeQuery(id+"F10.imprint","IMPRINT",EDGE,{"disambiguationData":[TD([[subQ2,1.0]])],"derivedFrom":subQ1}),1.0]])]});}
            var Q4;
            {var subQ0=sQuery(id+"F10.wireOp",EDGE,"E53");var subQ1=sQuery(id+"F10.wireOp",EDGE,"E47");var subQ2=makeQuery(id+"F10.imprint","INTERSECT",VERTEX,{"disambiguationData":[OD(0.0)],"derivedFrom":[subQ1,subQ0]});Q4=makeQuery(id+"F10.imprint","IMPRINT",FACE,{"disambiguationData":[TD([[makeQuery(id+"F10.imprint","IMPRINT",EDGE,{"disambiguationData":[TD([[subQ2,1.0]])],"derivedFrom":subQ1}),1.0]])]});}
            var Q5;
            {var subQ0=sQuery(id+"F10.wireOp",EDGE,"E53");var subQ1=sQuery(id+"F10.wireOp",EDGE,"E47");var subQ2=makeQuery(id+"F10.imprint","INTERSECT",VERTEX,{"disambiguationData":[OD(1.0)],"derivedFrom":[subQ1,subQ0]});Q5=makeQuery(id+"F10.imprint","IMPRINT",FACE,{"disambiguationData":[TD([[makeQuery(id+"F10.imprint","IMPRINT",EDGE,{"disambiguationData":[TD([[subQ2,-1.0]])],"derivedFrom":subQ1}),1.0]])]});}
            var Q6;
            {var subQ0=sQuery(id+"F10.wireOp",EDGE,"E53");var subQ1=sQuery(id+"F10.wireOp",EDGE,"E47");var subQ2=makeQuery(id+"F10.imprint","INTERSECT",VERTEX,{"disambiguationData":[OD(1.0)],"derivedFrom":[subQ1,subQ0]});Q6=makeQuery(id+"F10.imprint","IMPRINT",FACE,{"disambiguationData":[TD([[makeQuery(id+"F10.imprint","IMPRINT",EDGE,{"disambiguationData":[TD([[subQ2,-1.0]])],"derivedFrom":subQ1}),-1.0]])]});}
            var Q7;
            {var subQ5=sQuery(id+"F10.wireOp",EDGE,"E53");var subQ7=makeQuery(id+"F10.imprint","IMPRINT",VERTEX,{"derivedFrom":subQ5});Q7=makeQuery(id+"F10.imprint","IMPRINT",FACE,{"disambiguationData":[TD([[makeQuery(id+"F10.imprint","IMPRINT",EDGE,{"disambiguationData":[TD([[subQ7,1.0]])],"derivedFrom":subQ5}),1.0]])]});}
            var Q8;
            {var subQ0=sQuery(id+"F10.wireOp",EDGE,"E51");var subQ1=sQuery(id+"F10.wireOp",EDGE,"E47");var subQ2=makeQuery(id+"F10.imprint","INTERSECT",VERTEX,{"disambiguationData":[OD(0.0)],"derivedFrom":[subQ1,subQ0]});Q8=makeQuery(id+"F10.imprint","IMPRINT",FACE,{"disambiguationData":[TD([[makeQuery(id+"F10.imprint","IMPRINT",EDGE,{"disambiguationData":[TD([[subQ2,1.0]])],"derivedFrom":subQ1}),-1.0]])]});}
            var Q9;
            {var subQ0=sQuery(id+"F10.wireOp",EDGE,"E53");var subQ1=sQuery(id+"F10.wireOp",EDGE,"E47");var subQ2=makeQuery(id+"F10.imprint","INTERSECT",VERTEX,{"disambiguationData":[OD(0.0)],"derivedFrom":[subQ1,subQ0]});Q9=makeQuery(id+"F10.imprint","IMPRINT",FACE,{"disambiguationData":[TD([[makeQuery(id+"F10.imprint","IMPRINT",EDGE,{"disambiguationData":[TD([[subQ2,1.0]])],"derivedFrom":subQ1}),-1.0]])]});}
            extrude(context, id + "F20", {"entities" : qUnion([Q0, Q1, Q2, Q3, Q4, Q5, Q6, Q7, Q8, Q9]), "depth" : 22.02 * mm, "hasSecondDirection" : true, "secondDirectionOppositeDirection" : true, "secondDirectionDepth" : 14.63 * mm});
        }
        {
            var Q0;
            {var subQ5=sQuery(id+"F10.wireOp",EDGE,"E53");var subQ7=makeQuery(id+"F10.imprint","IMPRINT",VERTEX,{"derivedFrom":subQ5});Q0=makeQuery(id+"F10.imprint","IMPRINT",FACE,{"disambiguationData":[TD([[makeQuery(id+"F10.imprint","IMPRINT",EDGE,{"disambiguationData":[TD([[subQ7,1.0]])],"derivedFrom":subQ5}),1.0]])]});}
            var Q1;
            {var subQ0=sQuery(id+"F10.wireOp",EDGE,"E53");var subQ1=sQuery(id+"F10.wireOp",EDGE,"E47");var subQ2=makeQuery(id+"F10.imprint","INTERSECT",VERTEX,{"disambiguationData":[OD(1.0)],"derivedFrom":[subQ1,subQ0]});Q1=makeQuery(id+"F10.imprint","IMPRINT",FACE,{"disambiguationData":[TD([[makeQuery(id+"F10.imprint","IMPRINT",EDGE,{"disambiguationData":[TD([[subQ2,-1.0]])],"derivedFrom":subQ1}),-1.0]])]});}
            var Q2;
            {var subQ0=sQuery(id+"F10.wireOp",EDGE,"E53");var subQ1=sQuery(id+"F10.wireOp",EDGE,"E47");var subQ2=makeQuery(id+"F10.imprint","INTERSECT",VERTEX,{"disambiguationData":[OD(0.0)],"derivedFrom":[subQ1,subQ0]});Q2=makeQuery(id+"F10.imprint","IMPRINT",FACE,{"disambiguationData":[TD([[makeQuery(id+"F10.imprint","IMPRINT",EDGE,{"disambiguationData":[TD([[subQ2,1.0]])],"derivedFrom":subQ1}),-1.0]])]});}
            extrude(context, id + "F21", {"entities" : qUnion([Q0, Q1, Q2]), "operationType" : NewBodyOperationType.REMOVE, "oppositeDirection" : true, "depth" : 11.3 * mm, "hasSecondDirection" : true, "secondDirectionOppositeDirection" : true, "secondDirectionDepth" : 9.14 * mm});
        }
        {
            var Q0;
            {var subQ0=sQuery(id+"F10.wireOp",EDGE,"E53");var subQ1=makeQuery(id+"F10.imprint","IMPRINT",VERTEX,{"derivedFrom":subQ0});Q0=makeQuery(id+"F12.boolean.opBoolean","COPY",EDGE,{"derivedFrom":makeQuery(id+"F12.opExtrude","CAP_EDGE",EDGE,{"disambiguationData":[OSD([subQ0]),TDD([makeQuery(id+"F10.imprint","IMPRINT",EDGE,{"disambiguationData":[TD([[subQ1,1.0]])],"derivedFrom":subQ0}),makeQuery(id+"F10.imprint","IMPRINT",EDGE,{"disambiguationData":[TD([[subQ1,-1.0]])],"derivedFrom":subQ0})])],"isStart":false})});}
            var Q1;
            {var subQ0=sQuery(id+"F10.wireOp",EDGE,"E53");Q1=makeQuery(id+"F12.boolean.opBoolean","COPY",EDGE,{"derivedFrom":makeQuery(id+"F12.opExtrude","CAP_EDGE",EDGE,{"disambiguationData":[OSD([subQ0]),TDD([makeQuery(id+"F10.imprint","IMPRINT",EDGE,{"disambiguationData":[TD([[makeQuery(id+"F10.imprint","INTERSECT",VERTEX,{"disambiguationData":[OD(1.0)],"derivedFrom":[sQuery(id+"F10.wireOp",EDGE,"E50"),subQ0]}),1.0]])],"derivedFrom":subQ0})])],"isStart":false})});}
            var Q2;
            {var subQ0=sQuery(id+"F10.wireOp",EDGE,"E53");Q2=makeQuery(id+"F11.boolean.opBoolean","INTERSECT",EDGE,{"derivedFrom":[makeQuery(id+"F8.opExtrude","SWEPT_FACE",FACE,{"disambiguationData":[OSD([sQuery(id+"F7.wireOp",EDGE,"E18")])]}),makeQuery(id+"F11.opExtrude","SWEPT_FACE",FACE,{"disambiguationData":[OSD([subQ0]),TDD([makeQuery(id+"F10.imprint","IMPRINT",EDGE,{"disambiguationData":[TD([[makeQuery(id+"F10.imprint","INTERSECT",VERTEX,{"disambiguationData":[OD(1.0)],"derivedFrom":[sQuery(id+"F10.wireOp",EDGE,"E50"),subQ0]}),1.0]])],"derivedFrom":subQ0})])]})]});}
            var Q3;
            {var subQ0=sQuery(id+"F10.wireOp",EDGE,"E53");var subQ1=sQuery(id+"F10.wireOp",EDGE,"E50");var subQ3=makeQuery(id+"F11.boolean.opBoolean","COPY",FACE,{"derivedFrom":makeQuery(id+"F11.opExtrude","SWEPT_FACE",FACE,{"disambiguationData":[OSD([subQ0]),TDD([makeQuery(id+"F10.imprint","IMPRINT",EDGE,{"disambiguationData":[TD([[makeQuery(id+"F10.imprint","INTERSECT",VERTEX,{"disambiguationData":[OD(1.0)],"derivedFrom":[subQ1,subQ0]}),1.0]])],"derivedFrom":subQ0})])]})});var subQ5=sQuery(id+"F7.wireOp",EDGE,"E18");Q3=makeQuery(id+"F14.opChamfer","BLEND_EDGE",EDGE,{"blendedFrom":[makeQuery(id+"F13.boolean.opBoolean","INTERSECT",EDGE,{"derivedFrom":[makeQuery(id+"F12.boolean.opBoolean","SPLIT",FACE,{"disambiguationData":[TD([makeQuery(id+"F8.opExtrude","CAP_FACE",FACE,{"disambiguationData":[OSD([subQ5])],"isStart":true})])],"derivedFrom":makeQuery(id+"F8.opExtrude","SWEPT_FACE",FACE,{"disambiguationData":[OSD([subQ5])]})}),makeQuery(id+"F13.opExtrude","SWEPT_FACE",FACE,{"disambiguationData":[OSD([sQuery(id+"F9.wireOp",EDGE,"E37")])]})]}),subQ3],"blendedInto":[subQ3]});}
            var Q4;
            {var subQ0=sQuery(id+"F10.wireOp",EDGE,"E53");var subQ1=makeQuery(id+"F10.imprint","IMPRINT",VERTEX,{"derivedFrom":subQ0});Q4=makeQuery(id+"F11.boolean.opBoolean","INTERSECT",EDGE,{"derivedFrom":[makeQuery(id+"F8.opExtrude","SWEPT_FACE",FACE,{"disambiguationData":[OSD([sQuery(id+"F7.wireOp",EDGE,"E18")])]}),makeQuery(id+"F11.opExtrude","SWEPT_FACE",FACE,{"disambiguationData":[OSD([subQ0]),TDD([makeQuery(id+"F10.imprint","IMPRINT",EDGE,{"disambiguationData":[TD([[subQ1,1.0]])],"derivedFrom":subQ0}),makeQuery(id+"F10.imprint","IMPRINT",EDGE,{"disambiguationData":[TD([[subQ1,-1.0]])],"derivedFrom":subQ0})])]})]});}
            var Q5;
            {var subQ0=sQuery(id+"F10.wireOp",EDGE,"E53");var subQ1=makeQuery(id+"F10.imprint","IMPRINT",VERTEX,{"derivedFrom":subQ0});var subQ4=makeQuery(id+"F11.boolean.opBoolean","COPY",FACE,{"derivedFrom":makeQuery(id+"F11.opExtrude","SWEPT_FACE",FACE,{"disambiguationData":[OSD([subQ0]),TDD([makeQuery(id+"F10.imprint","IMPRINT",EDGE,{"disambiguationData":[TD([[subQ1,1.0]])],"derivedFrom":subQ0}),makeQuery(id+"F10.imprint","IMPRINT",EDGE,{"disambiguationData":[TD([[subQ1,-1.0]])],"derivedFrom":subQ0})])]})});var subQ5=sQuery(id+"F7.wireOp",EDGE,"E18");Q5=makeQuery(id+"F14.opChamfer","BLEND_EDGE",EDGE,{"blendedFrom":[makeQuery(id+"F13.boolean.opBoolean","INTERSECT",EDGE,{"derivedFrom":[makeQuery(id+"F12.boolean.opBoolean","SPLIT",FACE,{"disambiguationData":[TD([makeQuery(id+"F8.opExtrude","CAP_FACE",FACE,{"disambiguationData":[OSD([subQ5])],"isStart":true})])],"derivedFrom":makeQuery(id+"F8.opExtrude","SWEPT_FACE",FACE,{"disambiguationData":[OSD([subQ5])]})}),makeQuery(id+"F13.opExtrude","SWEPT_FACE",FACE,{"disambiguationData":[OSD([sQuery(id+"F9.wireOp",EDGE,"E37")])]})]}),subQ4],"blendedInto":[subQ4]});}
            var Q6;
            Q6=makeQuery(id+"F12.boolean.opBoolean","INTERSECT",EDGE,{"derivedFrom":[makeQuery(id+"F8.opExtrude","SWEPT_FACE",FACE,{"disambiguationData":[OSD([sQuery(id+"F7.wireOp",EDGE,"E18")])]}),makeQuery(id+"F12.opExtrude","CAP_FACE",FACE,{"disambiguationData":[OSD([sQuery(id+"F10.wireOp",EDGE,"E47"),sQuery(id+"F10.wireOp",EDGE,"E50"),sQuery(id+"F10.wireOp",EDGE,"E53")])],"isStart":true})]});
            fillet(context, id + "F22", {"entities" : qUnion([Q0, Q1, Q2, Q3, Q4, Q5, Q6]), "radius" : 0.25 * mm, "tangentPropagation" : true, "allowEdgeOverflow" : false});
        }
        {
            var Q0;
            Q0=makeQuery(id+"F20.opExtrude","SWEPT_BODY",BODY,{"disambiguationData":[OSD([sQuery(id+"F10.wireOp",EDGE,"E50")])]});
            var Q1;
            Q1=sQuery(id+"F7.wireOp",EDGE,"E20");
            circularPattern(context, id + "F23", {"entities" : qUnion([Q0]), "axis" : qUnion([Q1]), "angle" : 360 * degree, "instanceCount" : 3, "equalSpace" : true});
        }
        {
            var Q0;
            Q0=makeQuery(id+"F20.opExtrude","SWEPT_BODY",BODY,{"disambiguationData":[OSD([sQuery(id+"F10.wireOp",EDGE,"E50")])]});
            transform(context, id + "F24", {"entities" : qUnion([Q0]), "transformType" : TransformType.TRANSLATION_3D, "dx" : 0 * mm, "dy" : 0 * mm, "dz" : 12.7 * mm, "makeCopy" : false});
        }
        {
            var Q0;
            Q0=makeQuery(id+"F23.opPattern","COPY",BODY,{"derivedFrom":makeQuery(id+"F20.opExtrude","SWEPT_BODY",BODY,{"disambiguationData":[OSD([sQuery(id+"F10.wireOp",EDGE,"E50")])]}),"instanceName":"1"});
            transform(context, id + "F25", {"entities" : qUnion([Q0]), "transformType" : TransformType.TRANSLATION_3D, "dx" : 0 * mm, "dy" : 0 * mm, "dz" : 25.4 * mm, "makeCopy" : false});
        }
        {
            var Q0;
            Q0=makeQuery(id+"F20.opExtrude","SWEPT_BODY",BODY,{"disambiguationData":[OSD([sQuery(id+"F10.wireOp",EDGE,"E50")])]});
            var Q1;
            Q1=makeQuery(id+"F23.opPattern","COPY",BODY,{"derivedFrom":makeQuery(id+"F20.opExtrude","SWEPT_BODY",BODY,{"disambiguationData":[OSD([sQuery(id+"F10.wireOp",EDGE,"E50")])]}),"instanceName":"2"});
            var Q2;
            Q2=makeQuery(id+"F23.opPattern","COPY",BODY,{"derivedFrom":makeQuery(id+"F20.opExtrude","SWEPT_BODY",BODY,{"disambiguationData":[OSD([sQuery(id+"F10.wireOp",EDGE,"E50")])]}),"instanceName":"1"});
            var Q3;
            Q3=makeQuery(id+"F1.opExtrude","SWEPT_BODY",BODY,{"disambiguationData":[OSD([sQuery(id+"F0.wireOp",EDGE,"E0.0"),sQuery(id+"F0.wireOp",EDGE,"E0.1"),sQuery(id+"F0.wireOp",EDGE,"E0.2"),sQuery(id+"F0.wireOp",EDGE,"E0.3"),sQuery(id+"F0.wireOp",EDGE,"E0.4"),sQuery(id+"F0.wireOp",EDGE,"E0.5")])]});
            booleanBodies(context, id + "F26", {"operationType" : BooleanOperationType.SUBTRACTION, "tools" : qUnion([Q0, Q1, Q2]), "targets" : qUnion([Q3]), "keepTools" : true});
        }
        {
            var Q0;
            Q0=makeQuery(id+"F20.opExtrude","SWEPT_BODY",BODY,{"disambiguationData":[OSD([sQuery(id+"F10.wireOp",EDGE,"E50")])]});
            var Q1;
            Q1=makeQuery(id+"F23.opPattern","COPY",BODY,{"derivedFrom":makeQuery(id+"F20.opExtrude","SWEPT_BODY",BODY,{"disambiguationData":[OSD([sQuery(id+"F10.wireOp",EDGE,"E50")])]}),"instanceName":"1"});
            var Q2;
            Q2=makeQuery(id+"F23.opPattern","COPY",BODY,{"derivedFrom":makeQuery(id+"F20.opExtrude","SWEPT_BODY",BODY,{"disambiguationData":[OSD([sQuery(id+"F10.wireOp",EDGE,"E50")])]}),"instanceName":"2"});
            deleteBodies(context, id + "F27", {"entities" : qUnion([Q0, Q1, Q2])});
        }
    });
